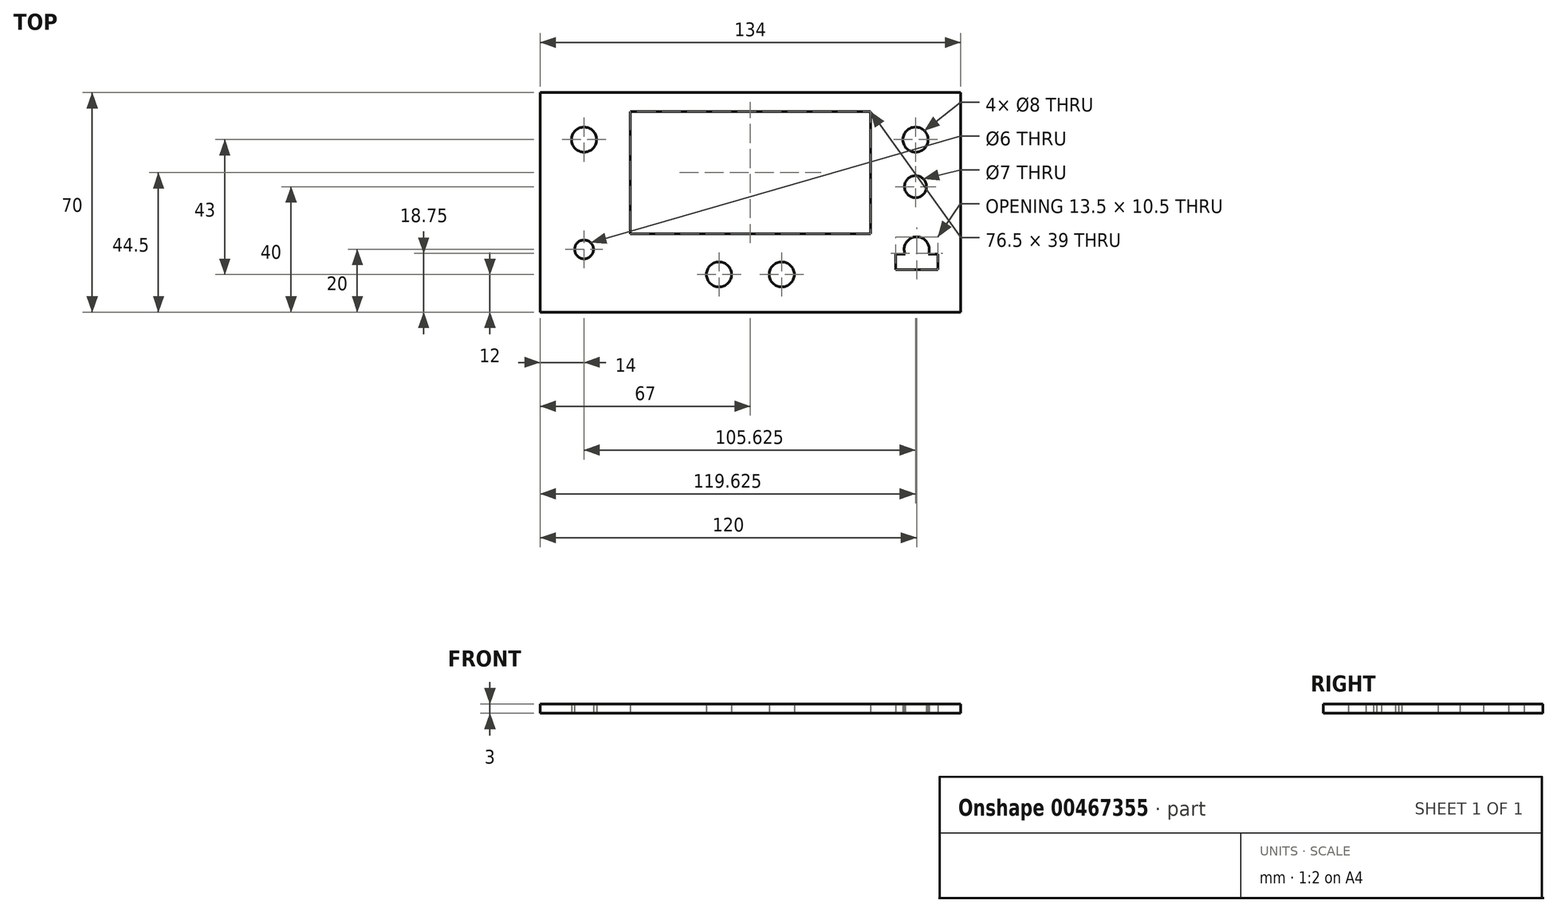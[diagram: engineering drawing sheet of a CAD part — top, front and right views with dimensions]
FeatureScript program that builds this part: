
annotation { "Feature Type Name" : "Feature", "Feature Type Description" : "" }
export const myFeature = defineFeature(function(context is Context, id is Id, definition is map)
    precondition{}
    {
        {
            var Q0;
            Q0=qCreatedBy(makeId("Top.planeOp"),FACE);
            var sketch = newSketch(context, id + "F0", { "sketchPlane" : qUnion([Q0])});
            skLineSegment(sketch, "E0.bottom", {"start": v(0, 0) * mm, "end": v(134, 0) * mm});
            skLineSegment(sketch, "E0.top", {"start": v(0, 70) * mm, "end": v(134, 70) * mm});
            skLineSegment(sketch, "E0.left", {"start": v(0, 0) * mm, "end": v(0, 70) * mm});
            skLineSegment(sketch, "E0.right", {"start": v(134, 0) * mm, "end": v(134, 70) * mm});
            skLineSegment(sketch, "E1", {"start": v(67, 70) * mm, "end": v(67, 0) * mm, "construction": true});
            skCircle(sketch, "E2", {"center": v(57, 12) * mm, "radius": 4 * mm});
            skCircle(sketch, "E3.MirrorC", {"center": v(77, 12) * mm, "radius": 4 * mm});
            skLineSegment(sketch, "E4.bottom", {"start": v(105.25, 64) * mm, "end": v(28.75, 64) * mm});
            skLineSegment(sketch, "E4.top", {"start": v(105.25, 25) * mm, "end": v(28.75, 25) * mm});
            skLineSegment(sketch, "E4.left", {"start": v(105.25, 64) * mm, "end": v(105.25, 25) * mm});
            skLineSegment(sketch, "E4.right", {"start": v(28.75, 64) * mm, "end": v(28.75, 25) * mm});
            skPoint(sketch, "E4.middle", {"position": v(67, 44.5) * mm});
            skCircle(sketch, "E5", {"center": v(119.63, 40) * mm, "radius": 3.5 * mm});
            skLineSegment(sketch, "E6.bottom", {"start": v(126.75, 13.5) * mm, "end": v(113.25, 13.5) * mm});
            skLineSegment(sketch, "E6.top", {"start": v(126.75, 18.5) * mm, "end": v(113.25, 18.5) * mm});
            skLineSegment(sketch, "E6.left", {"start": v(126.75, 13.5) * mm, "end": v(126.75, 18.5) * mm});
            skLineSegment(sketch, "E6.right", {"start": v(113.25, 13.5) * mm, "end": v(113.25, 18.5) * mm});
            skPoint(sketch, "E6.middle", {"position": v(120, 16) * mm});
            skCircle(sketch, "E7", {"center": v(14, 55) * mm, "radius": 4 * mm});
            skLineSegment(sketch, "E8", {"start": v(0, 35) * mm, "end": v(134, 35) * mm, "construction": true});
            skCircle(sketch, "E9.MirrorC", {"center": v(14, 20) * mm, "radius": 3 * mm});
            skCircle(sketch, "E10", {"center": v(120, 20) * mm, "radius": 4 * mm});
            skCircle(sketch, "E11", {"center": v(119.63, 55) * mm, "radius": 4 * mm});
            skLineSegment(sketch, "E12", {"start": v(119.63, 55) * mm, "end": v(119.63, 40) * mm, "construction": true});
            skSolve(sketch);
        }
        {
            var Q0;
            Q0=makeQuery(id+"F0.imprint","IMPRINT",FACE,{"disambiguationData":[TD([[makeQuery(id+"F0.imprint","IMPRINT",EDGE,{"derivedFrom":sQuery(id+"F0.wireOp",EDGE,"E0.bottom")}),1.0]])]});
            extrude(context, id + "F1", {"entities" : qUnion([Q0]), "depth" : 3 * mm});
        }
    });
